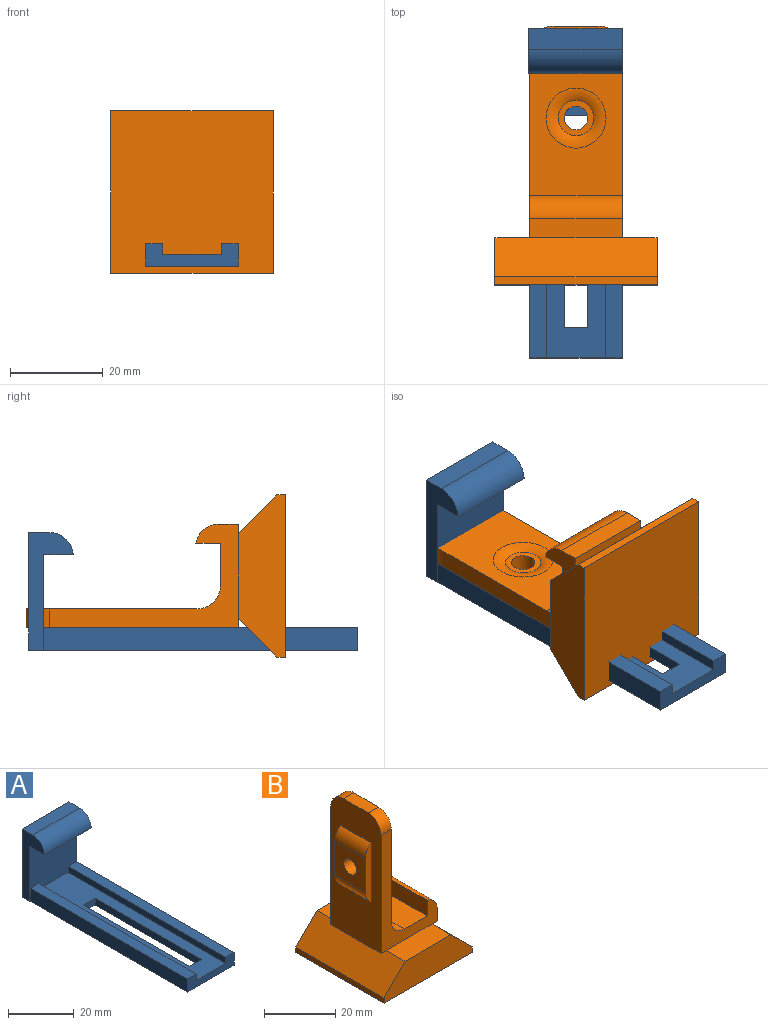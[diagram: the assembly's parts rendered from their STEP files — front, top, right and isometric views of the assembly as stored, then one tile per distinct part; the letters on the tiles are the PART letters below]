
ASSEMBLY  parts=2 mates=1
PART A: 20 faces, bbox 20.2x71.1x25.4 mm
  f0: plane 20.57x20.22mm, normal (0,-1,0), area 348.5mm2, adj f1,f2,f3,f4,f6,f12,f13,f14
  f1: plane 67.84x12.67mm, normal (0,0,1), area 627.6mm2, adj f0,f4,f7,f8,f9,f10,f11,f13
  f2: plane 67.84x4.83mm, normal (1,0,0), area 327.4mm2, adj f0,f11,f12,f14
  f3: plane 67.84x3.66mm, normal (0,0,1), area 248.1mm2, adj f0,f6,f11,f13
  f4: plane 67.84x2.29mm, normal (-1,0,0), area 155.1mm2, adj f0,f1,f11,f14
  f5: plane 25.4x20.22mm, normal (0,1,0), area 513.5mm2, adj f12,f15,f16,f17
  f6: plane 67.84x4.83mm, normal (-1,0,0), area 327.4mm2, adj f0,f3,f11,f12
  f7: plane 5.08x2.54mm, normal (0,-1,0), area 12.9mm2, adj f1,f8,f10,f12
  f8: plane 45.72x2.54mm, normal (-1,0,0), area 116.1mm2, adj f1,f7,f9,f12
  f9: plane 5.08x2.54mm, normal (0,1,0), area 12.9mm2, adj f1,f8,f10,f12
  f10: plane 45.72x2.54mm, normal (1,0,0), area 116.1mm2, adj f1,f7,f9,f12
  f11: plane 19.99x4.83mm, normal (0,-1,0), area 67.5mm2, adj f1,f2,f3,f4,f6,f12,f13,f14
  f12: plane 71.12x20.22mm, normal (0,0,-1), area 1190.2mm2, adj f0,f2,f5,f6,f7,f8,f9,f10
  f13: plane 67.84x2.29mm, normal (1,0,0), area 155.1mm2, adj f0,f1,f3,f11
  f14: plane 67.84x3.66mm, normal (0,0,1), area 248.1mm2, adj f0,f2,f4,f11
  f15: plane 25.4x9.63mm, normal (-1,0,0), area 108.4mm2, adj f0,f5,f12,f16,f18,f19
  f16: plane 20.22x4.55mm, normal (0,0,1), area 92.1mm2, adj f5,f15,f17,f19
  f17: plane 25.4x9.63mm, normal (1,0,0), area 108.4mm2, adj f0,f5,f12,f16,f18,f19
  f18: plane 20.22x6.35mm, normal (0,0,-1), area 128.4mm2, adj f0,f15,f17,f19
  f19: cylinder r=5.08mm len=20.22mm, axis (-1,0,0), area 156.2mm2, adj f15,f16,f17,f18
PART B: 31 faces, bbox 35x35x56 mm
  f0: plane 20x9.14mm, normal (0,0,1), area 182.9mm2, adj f12,f14,f18,f30
  f1: plane 18.24x7.5mm, normal (0,0,1), area 136.8mm2, adj f5,f8,f9,f12
  f2: plane 35x1.78mm, normal (-1,0,0), area 62.2mm2, adj f3,f5,f7,f8
  f3: plane 35x10.16mm, normal (0,-1,0), area 285.3mm2, adj f2,f4,f6,f7,f8,f9
  f4: plane 35x1.78mm, normal (1,0,0), area 62.2mm2, adj f3,f5,f7,f9
  f5: plane 35x10.16mm, normal (0,1,0), area 285.3mm2, adj f1,f2,f4,f7,f8,f9
  f6: plane 18.24x7.5mm, normal (0,0,1), area 136.8mm2, adj f3,f8,f9,f14
  f7: plane 35x35mm, normal (0,0,-1), area 1225mm2, adj f2,f3,f4,f5
  f8: plane 35x8.38mm, normal (-0.71,0,0.71), area 414.9mm2, adj f1,f2,f3,f5,f6,f10
  f9: plane 35x8.38mm, normal (0.71,0,0.71), area 414.9mm2, adj f1,f3,f4,f5,f6,f11
  f10: plane 20x2.06mm, normal (0,0,-1), area 41.2mm2, adj f8,f12,f13,f14
  f11: plane 20x2.06mm, normal (0,0,-1), area 41.2mm2, adj f9,f12,f14,f15
  f12: plane 40.73x22.35mm, normal (0,1,0), area 257.3mm2, adj f0,f1,f10,f11,f13,f15,f17,f18
  f13: plane 45.81x20mm, normal (-1,0,0), area 658.6mm2, adj f10,f12,f14,f16,f21,f22,f25,f26
  f14: plane 40.73x22.35mm, normal (0,-1,0), area 257.3mm2, adj f0,f6,f10,f11,f13,f15,f17,f18
  f15: plane 20x4.17mm, normal (1,0,0), area 83.3mm2, adj f11,f12,f14,f23
  f16: plane 9.84x4.06mm, normal (0,0,1), area 40mm2, adj f13,f17,f21,f22
  f17: plane 36.92x20mm, normal (1,0,0), area 595.2mm2, adj f12,f14,f16,f21,f22,f24,f30
  f18: plane 20x5.33mm, normal (-1,0,0), area 106.7mm2, adj f0,f12,f14,f23
  f19: cylinder r=2.54mm len=5.59mm, axis (1,0,0), area 89.2mm2, adj f20,f27
  f20: plane 7.62x7.62mm, normal (1,0,0), area 25.3mm2, adj f19,f24
  f21: cylinder r=5.08mm len=5.08mm, axis (1,0,0), area 32.4mm2, adj f12,f13,f16,f17
  f22: cylinder r=5.08mm len=5.08mm, axis (-1,0,0), area 32.4mm2, adj f13,f14,f16,f17
  f23: cylinder r=5.08mm len=20mm, axis (0,-1,0), area 139.1mm2, adj f12,f14,f15,f18
  f24: torus R=6.49mm, axis (-1,0,0), area 90.5mm2, adj f17,f20
  f25: plane 20.22x2.29mm, normal (0,-1,0), area 40.5mm2, adj f13,f27,f28,f29
  f26: plane 20.22x2.29mm, normal (0,1,0), area 40.5mm2, adj f13,f27,f28,f29
  f27: plane 12.19x11.73mm, normal (-1,0,0), area 122.8mm2, adj f19,f25,f26,f28,f29
  f28: cylinder r=5.08mm len=12.19mm, axis (0,1,0), area 61.2mm2, adj f13,f25,f26,f27
  f29: cylinder r=5.08mm len=12.19mm, axis (0,1,0), area 61.2mm2, adj f13,f25,f26,f27
  f30: cylinder r=5.08mm len=20mm, axis (0,-1,0), area 159.6mm2, adj f0,f12,f14,f17
PLACE A at identity
PLACE B rot(axis=(-0.58,-0.58,-0.58),120deg) t=(47.2,5.54,16)mm
MATE slider B.f10 <-> A.f11  axis (0,-1,0) through (37.2,15.7,4.83)mm
